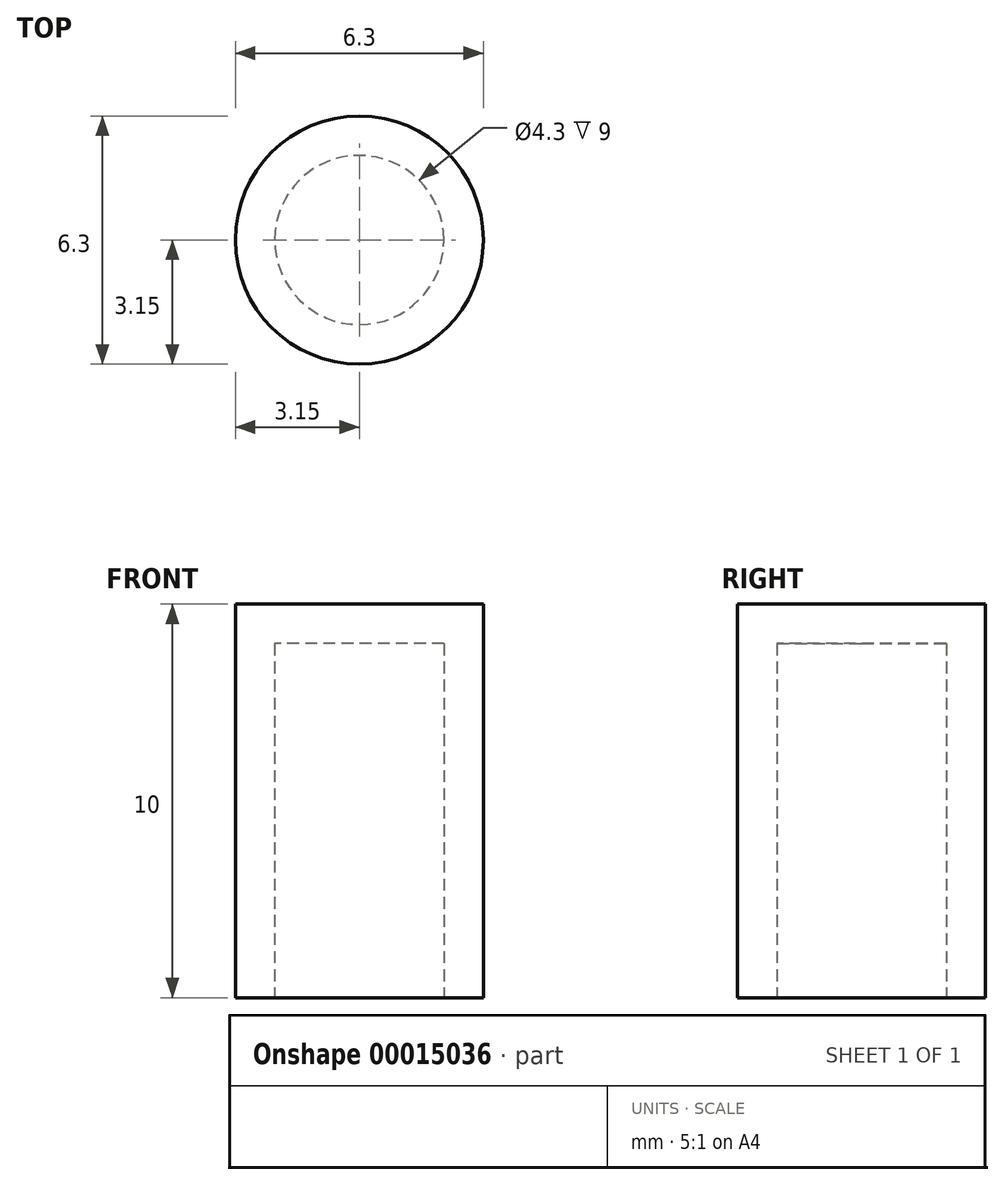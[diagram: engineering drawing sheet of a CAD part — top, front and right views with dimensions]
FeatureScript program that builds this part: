
annotation { "Feature Type Name" : "Feature", "Feature Type Description" : "" }
export const myFeature = defineFeature(function(context is Context, id is Id, definition is map)
    precondition{}
    {
        {
            var Q0;
            Q0=qCreatedBy(makeId("Top.planeOp"),FACE);
            var sketch = newSketch(context, id + "F0", { "sketchPlane" : qUnion([Q0])});
            skCircle(sketch, "E0", {"center": v(0, 0) * mm, "radius": 3.15 * mm});
            skCircle(sketch, "E1", {"center": v(0, 0) * mm, "radius": 2.15 * mm});
            skSolve(sketch);
        }
        {
            var Q0;
            Q0=qSketchRegion(id+"F0",true);
            extrude(context, id + "F1", {"entities" : qUnion([Q0]), "depth" : 9 * mm});
        }
        {
            var Q0;
            Q0=makeQuery(id+"F1.opExtrude","CAP_FACE",FACE,{"disambiguationData":[OSD([sQuery(id+"F0.wireOp",EDGE,"E0"),sQuery(id+"F0.wireOp",EDGE,"E1")])],"isStart":false});
            var sketch = newSketch(context, id + "F2", { "sketchPlane" : qUnion([Q0])});
            skCircle(sketch, "E2", {"center": v(0, 0) * mm, "radius": 3.15 * mm});
            skSolve(sketch);
        }
        {
            var Q0;
            Q0=qSketchRegion(id+"F2",true);
            extrude(context, id + "F3", {"entities" : qUnion([Q0]), "operationType" : NewBodyOperationType.ADD, "depth" : 1 * mm});
        }
    });
